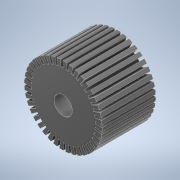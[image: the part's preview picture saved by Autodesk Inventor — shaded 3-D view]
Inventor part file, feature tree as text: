
AUTODESK INVENTOR PART (.ipt)
format: ipt  version: 2022 (Build 260153070, 153G)  size: 311,296 bytes
history: native  units: mm
features: sketch x4, extrude x2, hole x1
ambient origin geometry x8: Origin, YZ Plane, XZ Plane, XY Plane, X Axis, Y Axis, Z Axis, Center Point
bodies: Solid1 (feature_tree)
feature tree (7):
  extrude  "Extrusion1"  Depth=17.5mm TaperAngle=0.0deg
  extrude  "Extrusion2"  TaperAngle=0.0deg  [1 undecoded]
  hole  "Hole1"  [1 undecoded]
  sketch  "Sketch4"
  sketch  "Sketch1"  dims[d0=25.4mm d1=17.5mm d2=0.0mm]
  sketch  "Sketch2"  dims[d3=400.0mm d5=360.0deg d7=0.0mm d8=0.0mm]
  sketch  "Sketch3"  dims[d9=6.0mm d10=6.0mm d11=4.0mm d12=2.0mm d13=90.0deg d14=8.0mm d15=20.594885mm]
note: 2 required parameter values undecoded (feature->parameter linkage not recoverable at this tier; creation-order binding heuristic only, values carry confidence <= 0.55)
